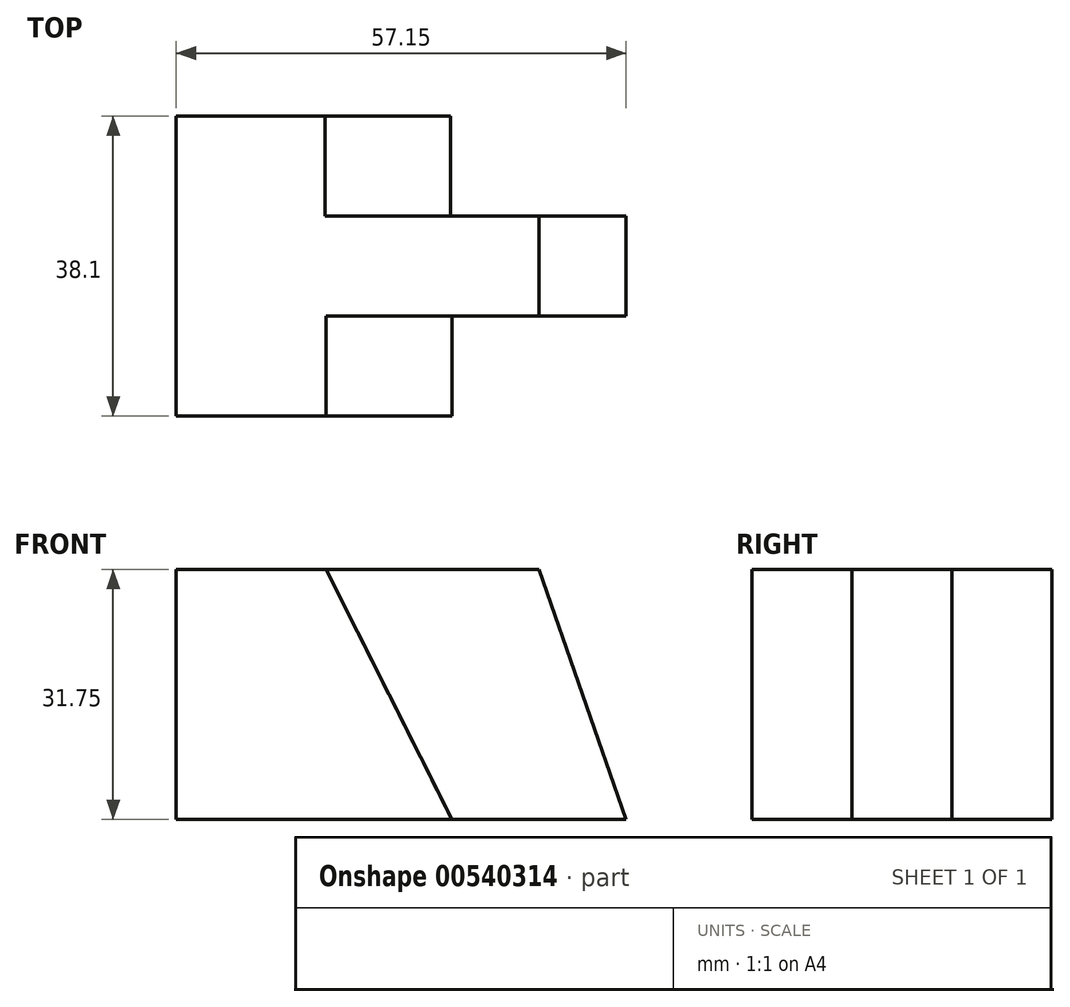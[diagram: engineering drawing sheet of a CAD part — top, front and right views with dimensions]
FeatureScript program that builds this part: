
annotation { "Feature Type Name" : "Feature", "Feature Type Description" : "" }
export const myFeature = defineFeature(function(context is Context, id is Id, definition is map)
    precondition{}
    {
        {
            var Q0;
            Q0=qCreatedBy(makeId("Front.planeOp"),FACE);
            var sketch = newSketch(context, id + "F0", { "sketchPlane" : qUnion([Q0])});
            skLineSegment(sketch, "E0.bottom", {"start": v(-57.15, 31.75) * mm, "end": v(0, 31.75) * mm});
            skLineSegment(sketch, "E0.top", {"start": v(-57.15, 0) * mm, "end": v(0, 0) * mm});
            skLineSegment(sketch, "E0.left", {"start": v(-57.15, 31.75) * mm, "end": v(-57.15, 0) * mm});
            skLineSegment(sketch, "E0.right", {"start": v(0, 31.75) * mm, "end": v(0, 0) * mm});
            skSolve(sketch);
        }
        {
            var Q0;
            Q0 = qSketchRegion(id + "F0", true);
            extrude(context, id + "F1", {"entities" : qUnion([Q0]), "depth" : 38.1 * mm, "offsetDistance" : 25.4 * mm});
        }
        {
            var Q0;
            Q0=makeQuery(id+"F1.opExtrude","CAP_FACE",FACE,{"disambiguationData":[OSD([sQuery(id+"F0.wireOp",EDGE,"E0.bottom"),sQuery(id+"F0.wireOp",EDGE,"E0.top"),sQuery(id+"F0.wireOp",EDGE,"E0.left"),sQuery(id+"F0.wireOp",EDGE,"E0.right")])],"isStart":false});
            var sketch = newSketch(context, id + "F2", { "sketchPlane" : qUnion([Q0])});
            skLineSegment(sketch, "E1", {"start": v(-57.15, 31.75) * mm, "end": v(-38.1, 31.75) * mm});
            skLineSegment(sketch, "E2", {"start": v(-38.1, 31.75) * mm, "end": v(-22.11, 0) * mm});
            skSolve(sketch);
        }
        {
            var Q0;
            {var subQ0=sQuery(id+"F2.wireOp",EDGE,"E2");Q0=makeQuery(id+"F2.imprint","IMPRINT",FACE,{"disambiguationData":[TD([[makeQuery(id+"F2.imprint","IMPRINT",EDGE,{"derivedFrom":subQ0}),1.0]])]});}
            extrude(context, id + "F3", {"entities" : qUnion([Q0]), "operationType" : NewBodyOperationType.REMOVE, "oppositeDirection" : true, "depth" : 12.7 * mm, "offsetDistance" : 25.4 * mm});
        }
        {
            var Q0;
            Q0=makeQuery(id+"F1.opExtrude","CAP_FACE",FACE,{"disambiguationData":[OSD([sQuery(id+"F0.wireOp",EDGE,"E0.bottom"),sQuery(id+"F0.wireOp",EDGE,"E0.top"),sQuery(id+"F0.wireOp",EDGE,"E0.left"),sQuery(id+"F0.wireOp",EDGE,"E0.right")])],"isStart":true});
            var sketch = newSketch(context, id + "F4", { "sketchPlane" : qUnion([Q0])});
            skLineSegment(sketch, "E3", {"start": v(38.24, 31.75) * mm, "end": v(22.29, 0) * mm});
            skSolve(sketch);
        }
        {
            var Q0;
            Q0 = qSketchRegion(id + "F4", true);
            var Q1;
            {var subQ0=sQuery(id+"F4.wireOp",EDGE,"E3");Q1=makeQuery(id+"F4.imprint","IMPRINT",FACE,{"disambiguationData":[TD([[makeQuery(id+"F4.imprint","IMPRINT",EDGE,{"derivedFrom":subQ0}),-1.0]])]});}
            extrude(context, id + "F5", {"entities" : qUnion([Q0, Q1]), "operationType" : NewBodyOperationType.REMOVE, "oppositeDirection" : true, "depth" : 12.7 * mm, "offsetDistance" : 25.4 * mm});
        }
        {
            var Q0;
            Q0=makeQuery(id+"F3.boolean.opBoolean","COPY",FACE,{"derivedFrom":makeQuery(id+"F3.opExtrude","CAP_FACE",FACE,{"disambiguationData":[OSD([sQuery(id+"F0.wireOp",EDGE,"E0.bottom"),sQuery(id+"F0.wireOp",EDGE,"E0.top"),sQuery(id+"F0.wireOp",EDGE,"E0.right"),sQuery(id+"F2.wireOp",EDGE,"E2")])],"isStart":false})});
            var sketch = newSketch(context, id + "F6", { "sketchPlane" : qUnion([Q0])});
            skLineSegment(sketch, "E4", {"start": v(0, 0) * mm, "end": v(-11.06, 31.75) * mm});
            skSolve(sketch);
        }
        {
            var Q0;
            Q0 = qSketchRegion(id + "F6", true);
            var Q1;
            {var subQ0=sQuery(id+"F6.wireOp",EDGE,"E4");Q1=makeQuery(id+"F6.imprint","IMPRINT",FACE,{"disambiguationData":[TD([[makeQuery(id+"F6.imprint","IMPRINT",EDGE,{"derivedFrom":subQ0}),-1.0]])]});}
            extrude(context, id + "F7", {"entities" : qUnion([Q0, Q1]), "operationType" : NewBodyOperationType.REMOVE, "oppositeDirection" : true, "depth" : 25.4 * mm, "offsetDistance" : 25.4 * mm});
        }
    });
